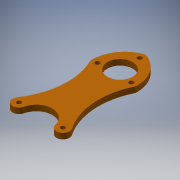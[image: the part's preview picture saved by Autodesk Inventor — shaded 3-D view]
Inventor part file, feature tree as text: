
AUTODESK INVENTOR PART (.ipt)
format: ipt  version: 2017 SP1 (Build 210196100, 196)  size: 152,064 bytes
history: native  units: in
note: dims shown in document units (in); Inventor stores cm internally (conversion verified against a paired STEP export)
features: extrude x1, sketch x1
ambient origin geometry x8: Origin, YZ Plane, XZ Plane, XY Plane, X Axis, Y Axis, Z Axis, Center Point
bodies: Solid1 (feature_tree)
feature tree (2):
  extrude  "Extrusion1"  Depth=0.25in
  sketch  "Sketch1"  dims[d0=1.125in d1=0.625in d3=0.196in d4=3.501in d5=4.0in d7=2.0in d8=0.2in d9=0.375in d10=1.5in d12=0.25in d15=0.25in d16=0.0in d18=1.125in d19=0.375in d20=60.0deg d23=1.375in d25=0.1875in d26=1.375in d27=1.0in]
